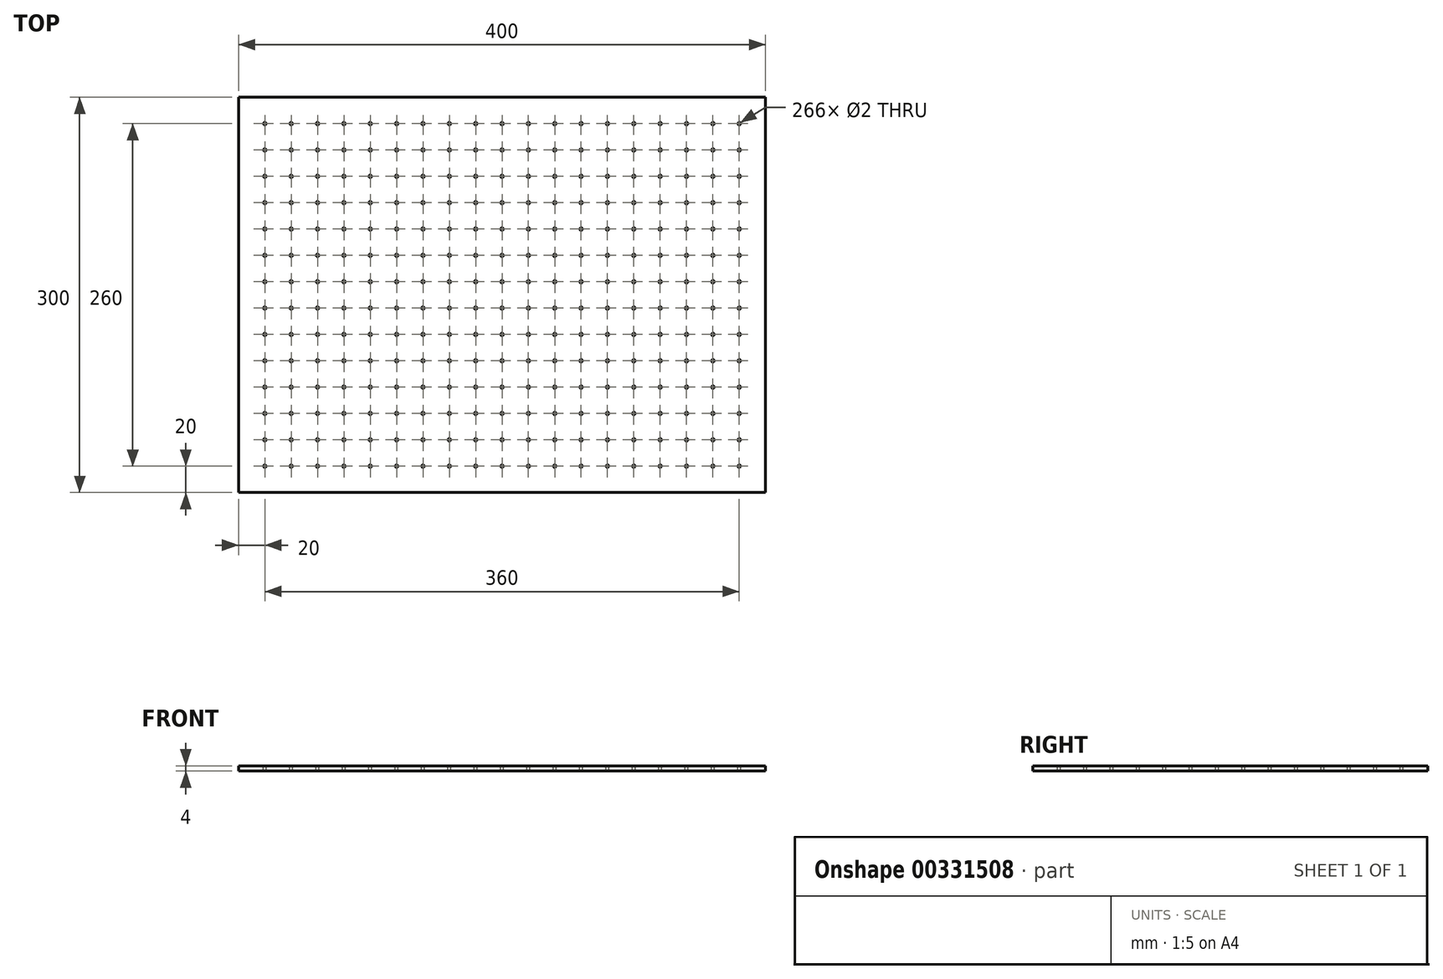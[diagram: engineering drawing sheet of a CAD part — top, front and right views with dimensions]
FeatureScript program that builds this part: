
annotation { "Feature Type Name" : "Feature", "Feature Type Description" : "" }
export const myFeature = defineFeature(function(context is Context, id is Id, definition is map)
    precondition{}
    {
        {
            var Q0;
            Q0=qCreatedBy(makeId("Top.planeOp"),FACE);
            var sketch = newSketch(context, id + "F0", { "sketchPlane" : qUnion([Q0])});
            skLineSegment(sketch, "E0.bottom", {"start": v(0, 0) * mm, "end": v(400, 0) * mm});
            skLineSegment(sketch, "E0.top", {"start": v(0, 300) * mm, "end": v(400, 300) * mm});
            skLineSegment(sketch, "E0.left", {"start": v(0, 0) * mm, "end": v(0, 300) * mm});
            skLineSegment(sketch, "E0.right", {"start": v(400, 0) * mm, "end": v(400, 300) * mm});
            skSolve(sketch);
        }
        {
            var Q0;
            Q0=makeQuery(id+"F0.imprint","IMPRINT",FACE,{"disambiguationData":[TD([[makeQuery(id+"F0.imprint","IMPRINT",EDGE,{"derivedFrom":sQuery(id+"F0.wireOp",EDGE,"E0.bottom")}),1.0]])]});
            extrude(context, id + "F1", {"entities" : qUnion([Q0]), "depth" : 4 * mm});
        }
        {
            var Q0;
            Q0=makeQuery(id+"F1.opExtrude","CAP_FACE",FACE,{"disambiguationData":[OSD([sQuery(id+"F0.wireOp",EDGE,"E0.bottom"),sQuery(id+"F0.wireOp",EDGE,"E0.top"),sQuery(id+"F0.wireOp",EDGE,"E0.left"),sQuery(id+"F0.wireOp",EDGE,"E0.right")])],"isStart":false});
            var sketch = newSketch(context, id + "F2", { "sketchPlane" : qUnion([Q0])});
            skCircle(sketch, "E1", {"center": v(20, 280) * mm, "radius": 1 * mm});
            skCircle(sketch, "E2.1.0.0", {"center": v(40, 280) * mm, "radius": 1 * mm});
            skCircle(sketch, "E2.2.0.0", {"center": v(60, 280) * mm, "radius": 1 * mm});
            skCircle(sketch, "E2.3.0.0", {"center": v(80, 280) * mm, "radius": 1 * mm});
            skCircle(sketch, "E2.4.0.0", {"center": v(100, 280) * mm, "radius": 1 * mm});
            skCircle(sketch, "E2.5.0.0", {"center": v(120, 280) * mm, "radius": 1 * mm});
            skCircle(sketch, "E2.6.0.0", {"center": v(140, 280) * mm, "radius": 1 * mm});
            skCircle(sketch, "E2.7.0.0", {"center": v(160, 280) * mm, "radius": 1 * mm});
            skCircle(sketch, "E2.8.0.0", {"center": v(180, 280) * mm, "radius": 1 * mm});
            skCircle(sketch, "E2.9.0.0", {"center": v(200, 280) * mm, "radius": 1 * mm});
            skCircle(sketch, "E2.10.0.0", {"center": v(220, 280) * mm, "radius": 1 * mm});
            skCircle(sketch, "E2.11.0.0", {"center": v(240, 280) * mm, "radius": 1 * mm});
            skCircle(sketch, "E2.12.0.0", {"center": v(260, 280) * mm, "radius": 1 * mm});
            skCircle(sketch, "E2.13.0.0", {"center": v(280, 280) * mm, "radius": 1 * mm});
            skCircle(sketch, "E2.14.0.0", {"center": v(300, 280) * mm, "radius": 1 * mm});
            skCircle(sketch, "E2.15.0.0", {"center": v(320, 280) * mm, "radius": 1 * mm});
            skCircle(sketch, "E2.16.0.0", {"center": v(340, 280) * mm, "radius": 1 * mm});
            skCircle(sketch, "E2.17.0.0", {"center": v(360, 280) * mm, "radius": 1 * mm});
            skCircle(sketch, "E2.18.0.0", {"center": v(380, 280) * mm, "radius": 1 * mm});
            skLineSegment(sketch, "E2.direction1", {"start": v(20, 280) * mm, "end": v(40, 280) * mm, "construction": true});
            skLineSegment(sketch, "E3.0.1.0", {"start": v(20, 260) * mm, "end": v(40, 260) * mm, "construction": true});
            skCircle(sketch, "E3.0.1.1", {"center": v(160, 260) * mm, "radius": 1 * mm});
            skCircle(sketch, "E3.0.1.2", {"center": v(180, 260) * mm, "radius": 1 * mm});
            skCircle(sketch, "E3.0.1.3", {"center": v(200, 260) * mm, "radius": 1 * mm});
            skCircle(sketch, "E3.0.1.4", {"center": v(220, 260) * mm, "radius": 1 * mm});
            skCircle(sketch, "E3.0.1.5", {"center": v(240, 260) * mm, "radius": 1 * mm});
            skCircle(sketch, "E3.0.1.6", {"center": v(260, 260) * mm, "radius": 1 * mm});
            skCircle(sketch, "E3.0.1.7", {"center": v(380, 260) * mm, "radius": 1 * mm});
            skCircle(sketch, "E3.0.1.8", {"center": v(340, 260) * mm, "radius": 1 * mm});
            skCircle(sketch, "E3.0.1.9", {"center": v(360, 260) * mm, "radius": 1 * mm});
            skCircle(sketch, "E3.0.1.10", {"center": v(280, 260) * mm, "radius": 1 * mm});
            skCircle(sketch, "E3.0.1.11", {"center": v(300, 260) * mm, "radius": 1 * mm});
            skCircle(sketch, "E3.0.1.12", {"center": v(320, 260) * mm, "radius": 1 * mm});
            skCircle(sketch, "E3.0.1.13", {"center": v(60, 260) * mm, "radius": 1 * mm});
            skCircle(sketch, "E3.0.1.14", {"center": v(80, 260) * mm, "radius": 1 * mm});
            skCircle(sketch, "E3.0.1.15", {"center": v(100, 260) * mm, "radius": 1 * mm});
            skCircle(sketch, "E3.0.1.16", {"center": v(120, 260) * mm, "radius": 1 * mm});
            skCircle(sketch, "E3.0.1.17", {"center": v(140, 260) * mm, "radius": 1 * mm});
            skCircle(sketch, "E3.0.1.18", {"center": v(20, 260) * mm, "radius": 1 * mm});
            skCircle(sketch, "E3.0.1.19", {"center": v(40, 260) * mm, "radius": 1 * mm});
            skLineSegment(sketch, "E3.0.2.0", {"start": v(20, 240) * mm, "end": v(40, 240) * mm, "construction": true});
            skCircle(sketch, "E3.0.2.1", {"center": v(160, 240) * mm, "radius": 1 * mm});
            skCircle(sketch, "E3.0.2.2", {"center": v(180, 240) * mm, "radius": 1 * mm});
            skCircle(sketch, "E3.0.2.3", {"center": v(200, 240) * mm, "radius": 1 * mm});
            skCircle(sketch, "E3.0.2.4", {"center": v(220, 240) * mm, "radius": 1 * mm});
            skCircle(sketch, "E3.0.2.5", {"center": v(240, 240) * mm, "radius": 1 * mm});
            skCircle(sketch, "E3.0.2.6", {"center": v(260, 240) * mm, "radius": 1 * mm});
            skCircle(sketch, "E3.0.2.7", {"center": v(380, 240) * mm, "radius": 1 * mm});
            skCircle(sketch, "E3.0.2.8", {"center": v(340, 240) * mm, "radius": 1 * mm});
            skCircle(sketch, "E3.0.2.9", {"center": v(360, 240) * mm, "radius": 1 * mm});
            skCircle(sketch, "E3.0.2.10", {"center": v(280, 240) * mm, "radius": 1 * mm});
            skCircle(sketch, "E3.0.2.11", {"center": v(300, 240) * mm, "radius": 1 * mm});
            skCircle(sketch, "E3.0.2.12", {"center": v(320, 240) * mm, "radius": 1 * mm});
            skCircle(sketch, "E3.0.2.13", {"center": v(60, 240) * mm, "radius": 1 * mm});
            skCircle(sketch, "E3.0.2.14", {"center": v(80, 240) * mm, "radius": 1 * mm});
            skCircle(sketch, "E3.0.2.15", {"center": v(100, 240) * mm, "radius": 1 * mm});
            skCircle(sketch, "E3.0.2.16", {"center": v(120, 240) * mm, "radius": 1 * mm});
            skCircle(sketch, "E3.0.2.17", {"center": v(140, 240) * mm, "radius": 1 * mm});
            skCircle(sketch, "E3.0.2.18", {"center": v(20, 240) * mm, "radius": 1 * mm});
            skCircle(sketch, "E3.0.2.19", {"center": v(40, 240) * mm, "radius": 1 * mm});
            skLineSegment(sketch, "E3.0.3.0", {"start": v(20, 220) * mm, "end": v(40, 220) * mm, "construction": true});
            skCircle(sketch, "E3.0.3.1", {"center": v(160, 220) * mm, "radius": 1 * mm});
            skCircle(sketch, "E3.0.3.2", {"center": v(180, 220) * mm, "radius": 1 * mm});
            skCircle(sketch, "E3.0.3.3", {"center": v(200, 220) * mm, "radius": 1 * mm});
            skCircle(sketch, "E3.0.3.4", {"center": v(220, 220) * mm, "radius": 1 * mm});
            skCircle(sketch, "E3.0.3.5", {"center": v(240, 220) * mm, "radius": 1 * mm});
            skCircle(sketch, "E3.0.3.6", {"center": v(260, 220) * mm, "radius": 1 * mm});
            skCircle(sketch, "E3.0.3.7", {"center": v(380, 220) * mm, "radius": 1 * mm});
            skCircle(sketch, "E3.0.3.8", {"center": v(340, 220) * mm, "radius": 1 * mm});
            skCircle(sketch, "E3.0.3.9", {"center": v(360, 220) * mm, "radius": 1 * mm});
            skCircle(sketch, "E3.0.3.10", {"center": v(280, 220) * mm, "radius": 1 * mm});
            skCircle(sketch, "E3.0.3.11", {"center": v(300, 220) * mm, "radius": 1 * mm});
            skCircle(sketch, "E3.0.3.12", {"center": v(320, 220) * mm, "radius": 1 * mm});
            skCircle(sketch, "E3.0.3.13", {"center": v(60, 220) * mm, "radius": 1 * mm});
            skCircle(sketch, "E3.0.3.14", {"center": v(80, 220) * mm, "radius": 1 * mm});
            skCircle(sketch, "E3.0.3.15", {"center": v(100, 220) * mm, "radius": 1 * mm});
            skCircle(sketch, "E3.0.3.16", {"center": v(120, 220) * mm, "radius": 1 * mm});
            skCircle(sketch, "E3.0.3.17", {"center": v(140, 220) * mm, "radius": 1 * mm});
            skCircle(sketch, "E3.0.3.18", {"center": v(20, 220) * mm, "radius": 1 * mm});
            skCircle(sketch, "E3.0.3.19", {"center": v(40, 220) * mm, "radius": 1 * mm});
            skLineSegment(sketch, "E3.0.4.0", {"start": v(20, 200) * mm, "end": v(40, 200) * mm, "construction": true});
            skCircle(sketch, "E3.0.4.1", {"center": v(160, 200) * mm, "radius": 1 * mm});
            skCircle(sketch, "E3.0.4.2", {"center": v(180, 200) * mm, "radius": 1 * mm});
            skCircle(sketch, "E3.0.4.3", {"center": v(200, 200) * mm, "radius": 1 * mm});
            skCircle(sketch, "E3.0.4.4", {"center": v(220, 200) * mm, "radius": 1 * mm});
            skCircle(sketch, "E3.0.4.5", {"center": v(240, 200) * mm, "radius": 1 * mm});
            skCircle(sketch, "E3.0.4.6", {"center": v(260, 200) * mm, "radius": 1 * mm});
            skCircle(sketch, "E3.0.4.7", {"center": v(380, 200) * mm, "radius": 1 * mm});
            skCircle(sketch, "E3.0.4.8", {"center": v(340, 200) * mm, "radius": 1 * mm});
            skCircle(sketch, "E3.0.4.9", {"center": v(360, 200) * mm, "radius": 1 * mm});
            skCircle(sketch, "E3.0.4.10", {"center": v(280, 200) * mm, "radius": 1 * mm});
            skCircle(sketch, "E3.0.4.11", {"center": v(300, 200) * mm, "radius": 1 * mm});
            skCircle(sketch, "E3.0.4.12", {"center": v(320, 200) * mm, "radius": 1 * mm});
            skCircle(sketch, "E3.0.4.13", {"center": v(60, 200) * mm, "radius": 1 * mm});
            skCircle(sketch, "E3.0.4.14", {"center": v(80, 200) * mm, "radius": 1 * mm});
            skCircle(sketch, "E3.0.4.15", {"center": v(100, 200) * mm, "radius": 1 * mm});
            skCircle(sketch, "E3.0.4.16", {"center": v(120, 200) * mm, "radius": 1 * mm});
            skCircle(sketch, "E3.0.4.17", {"center": v(140, 200) * mm, "radius": 1 * mm});
            skCircle(sketch, "E3.0.4.18", {"center": v(20, 200) * mm, "radius": 1 * mm});
            skCircle(sketch, "E3.0.4.19", {"center": v(40, 200) * mm, "radius": 1 * mm});
            skLineSegment(sketch, "E3.0.5.0", {"start": v(20, 180) * mm, "end": v(40, 180) * mm, "construction": true});
            skCircle(sketch, "E3.0.5.1", {"center": v(160, 180) * mm, "radius": 1 * mm});
            skCircle(sketch, "E3.0.5.2", {"center": v(180, 180) * mm, "radius": 1 * mm});
            skCircle(sketch, "E3.0.5.3", {"center": v(200, 180) * mm, "radius": 1 * mm});
            skCircle(sketch, "E3.0.5.4", {"center": v(220, 180) * mm, "radius": 1 * mm});
            skCircle(sketch, "E3.0.5.5", {"center": v(240, 180) * mm, "radius": 1 * mm});
            skCircle(sketch, "E3.0.5.6", {"center": v(260, 180) * mm, "radius": 1 * mm});
            skCircle(sketch, "E3.0.5.7", {"center": v(380, 180) * mm, "radius": 1 * mm});
            skCircle(sketch, "E3.0.5.8", {"center": v(340, 180) * mm, "radius": 1 * mm});
            skCircle(sketch, "E3.0.5.9", {"center": v(360, 180) * mm, "radius": 1 * mm});
            skCircle(sketch, "E3.0.5.10", {"center": v(280, 180) * mm, "radius": 1 * mm});
            skCircle(sketch, "E3.0.5.11", {"center": v(300, 180) * mm, "radius": 1 * mm});
            skCircle(sketch, "E3.0.5.12", {"center": v(320, 180) * mm, "radius": 1 * mm});
            skCircle(sketch, "E3.0.5.13", {"center": v(60, 180) * mm, "radius": 1 * mm});
            skCircle(sketch, "E3.0.5.14", {"center": v(80, 180) * mm, "radius": 1 * mm});
            skCircle(sketch, "E3.0.5.15", {"center": v(100, 180) * mm, "radius": 1 * mm});
            skCircle(sketch, "E3.0.5.16", {"center": v(120, 180) * mm, "radius": 1 * mm});
            skCircle(sketch, "E3.0.5.17", {"center": v(140, 180) * mm, "radius": 1 * mm});
            skCircle(sketch, "E3.0.5.18", {"center": v(20, 180) * mm, "radius": 1 * mm});
            skCircle(sketch, "E3.0.5.19", {"center": v(40, 180) * mm, "radius": 1 * mm});
            skLineSegment(sketch, "E3.0.6.0", {"start": v(20, 160) * mm, "end": v(40, 160) * mm, "construction": true});
            skCircle(sketch, "E3.0.6.1", {"center": v(160, 160) * mm, "radius": 1 * mm});
            skCircle(sketch, "E3.0.6.2", {"center": v(180, 160) * mm, "radius": 1 * mm});
            skCircle(sketch, "E3.0.6.3", {"center": v(200, 160) * mm, "radius": 1 * mm});
            skCircle(sketch, "E3.0.6.4", {"center": v(220, 160) * mm, "radius": 1 * mm});
            skCircle(sketch, "E3.0.6.5", {"center": v(240, 160) * mm, "radius": 1 * mm});
            skCircle(sketch, "E3.0.6.6", {"center": v(260, 160) * mm, "radius": 1 * mm});
            skCircle(sketch, "E3.0.6.7", {"center": v(380, 160) * mm, "radius": 1 * mm});
            skCircle(sketch, "E3.0.6.8", {"center": v(340, 160) * mm, "radius": 1 * mm});
            skCircle(sketch, "E3.0.6.9", {"center": v(360, 160) * mm, "radius": 1 * mm});
            skCircle(sketch, "E3.0.6.10", {"center": v(280, 160) * mm, "radius": 1 * mm});
            skCircle(sketch, "E3.0.6.11", {"center": v(300, 160) * mm, "radius": 1 * mm});
            skCircle(sketch, "E3.0.6.12", {"center": v(320, 160) * mm, "radius": 1 * mm});
            skCircle(sketch, "E3.0.6.13", {"center": v(60, 160) * mm, "radius": 1 * mm});
            skCircle(sketch, "E3.0.6.14", {"center": v(80, 160) * mm, "radius": 1 * mm});
            skCircle(sketch, "E3.0.6.15", {"center": v(100, 160) * mm, "radius": 1 * mm});
            skCircle(sketch, "E3.0.6.16", {"center": v(120, 160) * mm, "radius": 1 * mm});
            skCircle(sketch, "E3.0.6.17", {"center": v(140, 160) * mm, "radius": 1 * mm});
            skCircle(sketch, "E3.0.6.18", {"center": v(20, 160) * mm, "radius": 1 * mm});
            skCircle(sketch, "E3.0.6.19", {"center": v(40, 160) * mm, "radius": 1 * mm});
            skLineSegment(sketch, "E3.0.7.0", {"start": v(20, 140) * mm, "end": v(40, 140) * mm, "construction": true});
            skCircle(sketch, "E3.0.7.1", {"center": v(160, 140) * mm, "radius": 1 * mm});
            skCircle(sketch, "E3.0.7.2", {"center": v(180, 140) * mm, "radius": 1 * mm});
            skCircle(sketch, "E3.0.7.3", {"center": v(200, 140) * mm, "radius": 1 * mm});
            skCircle(sketch, "E3.0.7.4", {"center": v(220, 140) * mm, "radius": 1 * mm});
            skCircle(sketch, "E3.0.7.5", {"center": v(240, 140) * mm, "radius": 1 * mm});
            skCircle(sketch, "E3.0.7.6", {"center": v(260, 140) * mm, "radius": 1 * mm});
            skCircle(sketch, "E3.0.7.7", {"center": v(380, 140) * mm, "radius": 1 * mm});
            skCircle(sketch, "E3.0.7.8", {"center": v(340, 140) * mm, "radius": 1 * mm});
            skCircle(sketch, "E3.0.7.9", {"center": v(360, 140) * mm, "radius": 1 * mm});
            skCircle(sketch, "E3.0.7.10", {"center": v(280, 140) * mm, "radius": 1 * mm});
            skCircle(sketch, "E3.0.7.11", {"center": v(300, 140) * mm, "radius": 1 * mm});
            skCircle(sketch, "E3.0.7.12", {"center": v(320, 140) * mm, "radius": 1 * mm});
            skCircle(sketch, "E3.0.7.13", {"center": v(60, 140) * mm, "radius": 1 * mm});
            skCircle(sketch, "E3.0.7.14", {"center": v(80, 140) * mm, "radius": 1 * mm});
            skCircle(sketch, "E3.0.7.15", {"center": v(100, 140) * mm, "radius": 1 * mm});
            skCircle(sketch, "E3.0.7.16", {"center": v(120, 140) * mm, "radius": 1 * mm});
            skCircle(sketch, "E3.0.7.17", {"center": v(140, 140) * mm, "radius": 1 * mm});
            skCircle(sketch, "E3.0.7.18", {"center": v(20, 140) * mm, "radius": 1 * mm});
            skCircle(sketch, "E3.0.7.19", {"center": v(40, 140) * mm, "radius": 1 * mm});
            skLineSegment(sketch, "E3.0.8.0", {"start": v(20, 120) * mm, "end": v(40, 120) * mm, "construction": true});
            skCircle(sketch, "E3.0.8.1", {"center": v(160, 120) * mm, "radius": 1 * mm});
            skCircle(sketch, "E3.0.8.2", {"center": v(180, 120) * mm, "radius": 1 * mm});
            skCircle(sketch, "E3.0.8.3", {"center": v(200, 120) * mm, "radius": 1 * mm});
            skCircle(sketch, "E3.0.8.4", {"center": v(220, 120) * mm, "radius": 1 * mm});
            skCircle(sketch, "E3.0.8.5", {"center": v(240, 120) * mm, "radius": 1 * mm});
            skCircle(sketch, "E3.0.8.6", {"center": v(260, 120) * mm, "radius": 1 * mm});
            skCircle(sketch, "E3.0.8.7", {"center": v(380, 120) * mm, "radius": 1 * mm});
            skCircle(sketch, "E3.0.8.8", {"center": v(340, 120) * mm, "radius": 1 * mm});
            skCircle(sketch, "E3.0.8.9", {"center": v(360, 120) * mm, "radius": 1 * mm});
            skCircle(sketch, "E3.0.8.10", {"center": v(280, 120) * mm, "radius": 1 * mm});
            skCircle(sketch, "E3.0.8.11", {"center": v(300, 120) * mm, "radius": 1 * mm});
            skCircle(sketch, "E3.0.8.12", {"center": v(320, 120) * mm, "radius": 1 * mm});
            skCircle(sketch, "E3.0.8.13", {"center": v(60, 120) * mm, "radius": 1 * mm});
            skCircle(sketch, "E3.0.8.14", {"center": v(80, 120) * mm, "radius": 1 * mm});
            skCircle(sketch, "E3.0.8.15", {"center": v(100, 120) * mm, "radius": 1 * mm});
            skCircle(sketch, "E3.0.8.16", {"center": v(120, 120) * mm, "radius": 1 * mm});
            skCircle(sketch, "E3.0.8.17", {"center": v(140, 120) * mm, "radius": 1 * mm});
            skCircle(sketch, "E3.0.8.18", {"center": v(20, 120) * mm, "radius": 1 * mm});
            skCircle(sketch, "E3.0.8.19", {"center": v(40, 120) * mm, "radius": 1 * mm});
            skLineSegment(sketch, "E3.0.9.0", {"start": v(20, 100) * mm, "end": v(40, 100) * mm, "construction": true});
            skCircle(sketch, "E3.0.9.1", {"center": v(160, 100) * mm, "radius": 1 * mm});
            skCircle(sketch, "E3.0.9.2", {"center": v(180, 100) * mm, "radius": 1 * mm});
            skCircle(sketch, "E3.0.9.3", {"center": v(200, 100) * mm, "radius": 1 * mm});
            skCircle(sketch, "E3.0.9.4", {"center": v(220, 100) * mm, "radius": 1 * mm});
            skCircle(sketch, "E3.0.9.5", {"center": v(240, 100) * mm, "radius": 1 * mm});
            skCircle(sketch, "E3.0.9.6", {"center": v(260, 100) * mm, "radius": 1 * mm});
            skCircle(sketch, "E3.0.9.7", {"center": v(380, 100) * mm, "radius": 1 * mm});
            skCircle(sketch, "E3.0.9.8", {"center": v(340, 100) * mm, "radius": 1 * mm});
            skCircle(sketch, "E3.0.9.9", {"center": v(360, 100) * mm, "radius": 1 * mm});
            skCircle(sketch, "E3.0.9.10", {"center": v(280, 100) * mm, "radius": 1 * mm});
            skCircle(sketch, "E3.0.9.11", {"center": v(300, 100) * mm, "radius": 1 * mm});
            skCircle(sketch, "E3.0.9.12", {"center": v(320, 100) * mm, "radius": 1 * mm});
            skCircle(sketch, "E3.0.9.13", {"center": v(60, 100) * mm, "radius": 1 * mm});
            skCircle(sketch, "E3.0.9.14", {"center": v(80, 100) * mm, "radius": 1 * mm});
            skCircle(sketch, "E3.0.9.15", {"center": v(100, 100) * mm, "radius": 1 * mm});
            skCircle(sketch, "E3.0.9.16", {"center": v(120, 100) * mm, "radius": 1 * mm});
            skCircle(sketch, "E3.0.9.17", {"center": v(140, 100) * mm, "radius": 1 * mm});
            skCircle(sketch, "E3.0.9.18", {"center": v(20, 100) * mm, "radius": 1 * mm});
            skCircle(sketch, "E3.0.9.19", {"center": v(40, 100) * mm, "radius": 1 * mm});
            skLineSegment(sketch, "E3.0.10.0", {"start": v(20, 80) * mm, "end": v(40, 80) * mm, "construction": true});
            skCircle(sketch, "E3.0.10.1", {"center": v(160, 80) * mm, "radius": 1 * mm});
            skCircle(sketch, "E3.0.10.2", {"center": v(180, 80) * mm, "radius": 1 * mm});
            skCircle(sketch, "E3.0.10.3", {"center": v(200, 80) * mm, "radius": 1 * mm});
            skCircle(sketch, "E3.0.10.4", {"center": v(220, 80) * mm, "radius": 1 * mm});
            skCircle(sketch, "E3.0.10.5", {"center": v(240, 80) * mm, "radius": 1 * mm});
            skCircle(sketch, "E3.0.10.6", {"center": v(260, 80) * mm, "radius": 1 * mm});
            skCircle(sketch, "E3.0.10.7", {"center": v(380, 80) * mm, "radius": 1 * mm});
            skCircle(sketch, "E3.0.10.8", {"center": v(340, 80) * mm, "radius": 1 * mm});
            skCircle(sketch, "E3.0.10.9", {"center": v(360, 80) * mm, "radius": 1 * mm});
            skCircle(sketch, "E3.0.10.10", {"center": v(280, 80) * mm, "radius": 1 * mm});
            skCircle(sketch, "E3.0.10.11", {"center": v(300, 80) * mm, "radius": 1 * mm});
            skCircle(sketch, "E3.0.10.12", {"center": v(320, 80) * mm, "radius": 1 * mm});
            skCircle(sketch, "E3.0.10.13", {"center": v(60, 80) * mm, "radius": 1 * mm});
            skCircle(sketch, "E3.0.10.14", {"center": v(80, 80) * mm, "radius": 1 * mm});
            skCircle(sketch, "E3.0.10.15", {"center": v(100, 80) * mm, "radius": 1 * mm});
            skCircle(sketch, "E3.0.10.16", {"center": v(120, 80) * mm, "radius": 1 * mm});
            skCircle(sketch, "E3.0.10.17", {"center": v(140, 80) * mm, "radius": 1 * mm});
            skCircle(sketch, "E3.0.10.18", {"center": v(20, 80) * mm, "radius": 1 * mm});
            skCircle(sketch, "E3.0.10.19", {"center": v(40, 80) * mm, "radius": 1 * mm});
            skLineSegment(sketch, "E3.0.11.0", {"start": v(20, 60) * mm, "end": v(40, 60) * mm, "construction": true});
            skCircle(sketch, "E3.0.11.1", {"center": v(160, 60) * mm, "radius": 1 * mm});
            skCircle(sketch, "E3.0.11.2", {"center": v(180, 60) * mm, "radius": 1 * mm});
            skCircle(sketch, "E3.0.11.3", {"center": v(200, 60) * mm, "radius": 1 * mm});
            skCircle(sketch, "E3.0.11.4", {"center": v(220, 60) * mm, "radius": 1 * mm});
            skCircle(sketch, "E3.0.11.5", {"center": v(240, 60) * mm, "radius": 1 * mm});
            skCircle(sketch, "E3.0.11.6", {"center": v(260, 60) * mm, "radius": 1 * mm});
            skCircle(sketch, "E3.0.11.7", {"center": v(380, 60) * mm, "radius": 1 * mm});
            skCircle(sketch, "E3.0.11.8", {"center": v(340, 60) * mm, "radius": 1 * mm});
            skCircle(sketch, "E3.0.11.9", {"center": v(360, 60) * mm, "radius": 1 * mm});
            skCircle(sketch, "E3.0.11.10", {"center": v(280, 60) * mm, "radius": 1 * mm});
            skCircle(sketch, "E3.0.11.11", {"center": v(300, 60) * mm, "radius": 1 * mm});
            skCircle(sketch, "E3.0.11.12", {"center": v(320, 60) * mm, "radius": 1 * mm});
            skCircle(sketch, "E3.0.11.13", {"center": v(60, 60) * mm, "radius": 1 * mm});
            skCircle(sketch, "E3.0.11.14", {"center": v(80, 60) * mm, "radius": 1 * mm});
            skCircle(sketch, "E3.0.11.15", {"center": v(100, 60) * mm, "radius": 1 * mm});
            skCircle(sketch, "E3.0.11.16", {"center": v(120, 60) * mm, "radius": 1 * mm});
            skCircle(sketch, "E3.0.11.17", {"center": v(140, 60) * mm, "radius": 1 * mm});
            skCircle(sketch, "E3.0.11.18", {"center": v(20, 60) * mm, "radius": 1 * mm});
            skCircle(sketch, "E3.0.11.19", {"center": v(40, 60) * mm, "radius": 1 * mm});
            skLineSegment(sketch, "E3.0.12.0", {"start": v(20, 40) * mm, "end": v(40, 40) * mm, "construction": true});
            skCircle(sketch, "E3.0.12.1", {"center": v(160, 40) * mm, "radius": 1 * mm});
            skCircle(sketch, "E3.0.12.2", {"center": v(180, 40) * mm, "radius": 1 * mm});
            skCircle(sketch, "E3.0.12.3", {"center": v(200, 40) * mm, "radius": 1 * mm});
            skCircle(sketch, "E3.0.12.4", {"center": v(220, 40) * mm, "radius": 1 * mm});
            skCircle(sketch, "E3.0.12.5", {"center": v(240, 40) * mm, "radius": 1 * mm});
            skCircle(sketch, "E3.0.12.6", {"center": v(260, 40) * mm, "radius": 1 * mm});
            skCircle(sketch, "E3.0.12.7", {"center": v(380, 40) * mm, "radius": 1 * mm});
            skCircle(sketch, "E3.0.12.8", {"center": v(340, 40) * mm, "radius": 1 * mm});
            skCircle(sketch, "E3.0.12.9", {"center": v(360, 40) * mm, "radius": 1 * mm});
            skCircle(sketch, "E3.0.12.10", {"center": v(280, 40) * mm, "radius": 1 * mm});
            skCircle(sketch, "E3.0.12.11", {"center": v(300, 40) * mm, "radius": 1 * mm});
            skCircle(sketch, "E3.0.12.12", {"center": v(320, 40) * mm, "radius": 1 * mm});
            skCircle(sketch, "E3.0.12.13", {"center": v(60, 40) * mm, "radius": 1 * mm});
            skCircle(sketch, "E3.0.12.14", {"center": v(80, 40) * mm, "radius": 1 * mm});
            skCircle(sketch, "E3.0.12.15", {"center": v(100, 40) * mm, "radius": 1 * mm});
            skCircle(sketch, "E3.0.12.16", {"center": v(120, 40) * mm, "radius": 1 * mm});
            skCircle(sketch, "E3.0.12.17", {"center": v(140, 40) * mm, "radius": 1 * mm});
            skCircle(sketch, "E3.0.12.18", {"center": v(20, 40) * mm, "radius": 1 * mm});
            skCircle(sketch, "E3.0.12.19", {"center": v(40, 40) * mm, "radius": 1 * mm});
            skLineSegment(sketch, "E3.0.13.0", {"start": v(20, 20) * mm, "end": v(40, 20) * mm, "construction": true});
            skCircle(sketch, "E3.0.13.1", {"center": v(160, 20) * mm, "radius": 1 * mm});
            skCircle(sketch, "E3.0.13.2", {"center": v(180, 20) * mm, "radius": 1 * mm});
            skCircle(sketch, "E3.0.13.3", {"center": v(200, 20) * mm, "radius": 1 * mm});
            skCircle(sketch, "E3.0.13.4", {"center": v(220, 20) * mm, "radius": 1 * mm});
            skCircle(sketch, "E3.0.13.5", {"center": v(240, 20) * mm, "radius": 1 * mm});
            skCircle(sketch, "E3.0.13.6", {"center": v(260, 20) * mm, "radius": 1 * mm});
            skCircle(sketch, "E3.0.13.7", {"center": v(380, 20) * mm, "radius": 1 * mm});
            skCircle(sketch, "E3.0.13.8", {"center": v(340, 20) * mm, "radius": 1 * mm});
            skCircle(sketch, "E3.0.13.9", {"center": v(360, 20) * mm, "radius": 1 * mm});
            skCircle(sketch, "E3.0.13.10", {"center": v(280, 20) * mm, "radius": 1 * mm});
            skCircle(sketch, "E3.0.13.11", {"center": v(300, 20) * mm, "radius": 1 * mm});
            skCircle(sketch, "E3.0.13.12", {"center": v(320, 20) * mm, "radius": 1 * mm});
            skCircle(sketch, "E3.0.13.13", {"center": v(60, 20) * mm, "radius": 1 * mm});
            skCircle(sketch, "E3.0.13.14", {"center": v(80, 20) * mm, "radius": 1 * mm});
            skCircle(sketch, "E3.0.13.15", {"center": v(100, 20) * mm, "radius": 1 * mm});
            skCircle(sketch, "E3.0.13.16", {"center": v(120, 20) * mm, "radius": 1 * mm});
            skCircle(sketch, "E3.0.13.17", {"center": v(140, 20) * mm, "radius": 1 * mm});
            skCircle(sketch, "E3.0.13.18", {"center": v(20, 20) * mm, "radius": 1 * mm});
            skCircle(sketch, "E3.0.13.19", {"center": v(40, 20) * mm, "radius": 1 * mm});
            skLineSegment(sketch, "E3.direction1", {"start": v(20, 280) * mm, "end": v(46, 280) * mm, "construction": true});
            skLineSegment(sketch, "E3.direction2", {"start": v(20, 280) * mm, "end": v(20, 260) * mm, "construction": true});
            skSolve(sketch);
        }
        {
            var Q0;
            Q0 = qSketchRegion(id + "F2", true);
            extrude(context, id + "F3", {"entities" : qUnion([Q0]), "operationType" : NewBodyOperationType.REMOVE, "endBound" : BoundingType.THROUGH_ALL, "oppositeDirection" : true, "depth" : 25 * mm});
        }
    });
